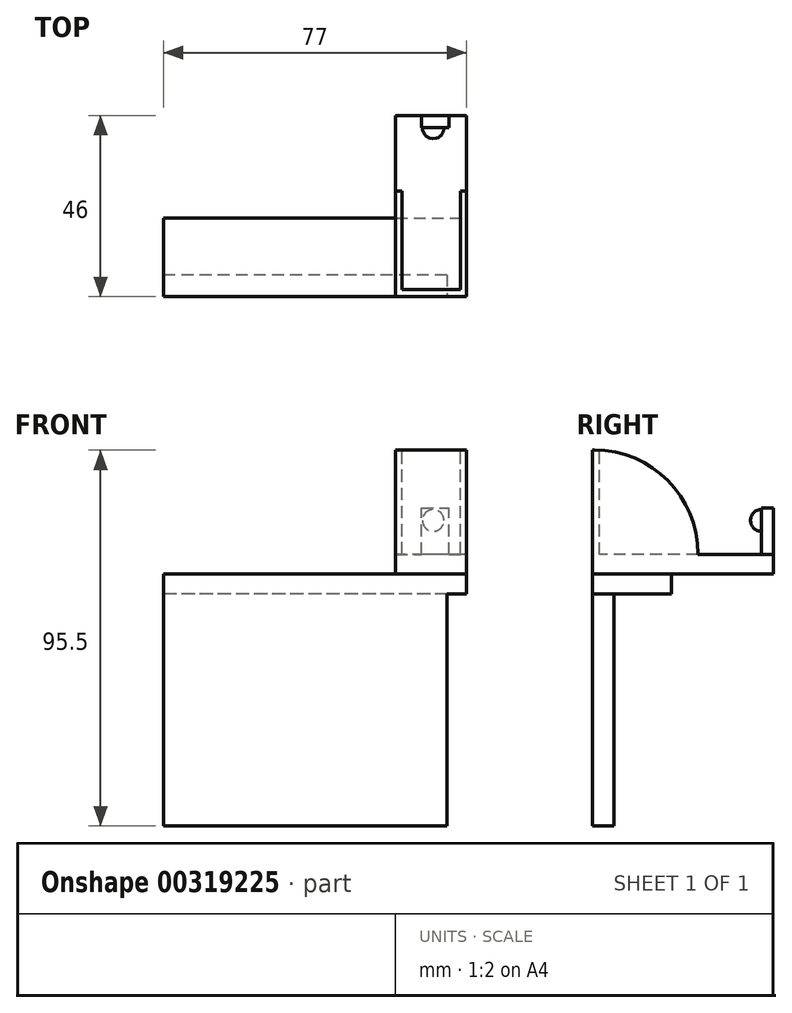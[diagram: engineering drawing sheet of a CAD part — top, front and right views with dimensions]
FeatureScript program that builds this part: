
annotation { "Feature Type Name" : "Feature", "Feature Type Description" : "" }
export const myFeature = defineFeature(function(context is Context, id is Id, definition is map)
    precondition{}
    {
        {
            var Q0;
            Q0=qCreatedBy(makeId("Top.planeOp"),FACE);
            var sketch = newSketch(context, id + "F0", { "sketchPlane" : qUnion([Q0])});
            skLineSegment(sketch, "E0.bottom", {"start": v(35.26, 25.04) * mm, "end": v(53.26, 25.04) * mm});
            skLineSegment(sketch, "E0.top", {"start": v(35.26, -20.96) * mm, "end": v(53.26, -20.96) * mm});
            skLineSegment(sketch, "E0.left", {"start": v(35.26, 25.04) * mm, "end": v(35.26, -20.96) * mm});
            skLineSegment(sketch, "E0.right", {"start": v(53.26, 25.04) * mm, "end": v(53.26, -20.96) * mm});
            skSolve(sketch);
        }
        {
            var Q0;
            Q0 = qSketchRegion(id + "F0", true);
            extrude(context, id + "F1", {"entities" : qUnion([Q0]), "depth" : 5 * mm});
        }
        {
            var Q0;
            Q0=makeQuery(id+"F1.opExtrude","CAP_FACE",FACE,{"disambiguationData":[OSD([sQuery(id+"F0.wireOp",EDGE,"E0.bottom"),sQuery(id+"F0.wireOp",EDGE,"E0.top"),sQuery(id+"F0.wireOp",EDGE,"E0.left"),sQuery(id+"F0.wireOp",EDGE,"E0.right")])],"isStart":false});
            var sketch = newSketch(context, id + "F2", { "sketchPlane" : qUnion([Q0])});
            skLineSegment(sketch, "E1.bottom", {"start": v(53.26, -20.96) * mm, "end": v(35.26, -20.96) * mm});
            skLineSegment(sketch, "E1.top", {"start": v(53.26, -19.13) * mm, "end": v(35.26, -19.13) * mm});
            skLineSegment(sketch, "E1.left", {"start": v(53.26, -20.96) * mm, "end": v(53.26, -19.13) * mm});
            skLineSegment(sketch, "E1.right", {"start": v(35.26, -20.96) * mm, "end": v(35.26, -19.13) * mm});
            skSolve(sketch);
        }
        {
            var Q0;
            Q0=makeQuery(id+"F2.imprint","IMPRINT",FACE,{"disambiguationData":[TD([[makeQuery(id+"F2.imprint","IMPRINT",EDGE,{"derivedFrom":sQuery(id+"F2.wireOp",EDGE,"E1.bottom")}),1.0]])]});
            extrude(context, id + "F3", {"entities" : qUnion([Q0]), "operationType" : NewBodyOperationType.ADD, "depth" : 26.5 * mm});
        }
        {
            var Q0;
            Q0=makeQuery(id+"F3.opExtrude","SWEPT_FACE",FACE,{"disambiguationData":[OSD([sQuery(id+"F2.wireOp",EDGE,"E1.top")])]});
            var sketch = newSketch(context, id + "F4", { "sketchPlane" : qUnion([Q0])});
            skLineSegment(sketch, "E2.bottom", {"start": v(-35.26, 5) * mm, "end": v(-36.8, 5) * mm});
            skLineSegment(sketch, "E2.top", {"start": v(-35.26, 31.5) * mm, "end": v(-36.8, 31.5) * mm});
            skLineSegment(sketch, "E2.left", {"start": v(-35.26, 5) * mm, "end": v(-35.26, 31.5) * mm});
            skLineSegment(sketch, "E2.right", {"start": v(-36.8, 5) * mm, "end": v(-36.8, 31.5) * mm});
            skLineSegment(sketch, "E3.bottom", {"start": v(-53.26, 5) * mm, "end": v(-51.68, 5) * mm});
            skLineSegment(sketch, "E3.top", {"start": v(-53.26, 31.5) * mm, "end": v(-51.68, 31.5) * mm});
            skLineSegment(sketch, "E3.left", {"start": v(-53.26, 5) * mm, "end": v(-53.26, 31.5) * mm});
            skLineSegment(sketch, "E3.right", {"start": v(-51.68, 5) * mm, "end": v(-51.68, 31.5) * mm});
            skSolve(sketch);
        }
        {
            var Q0;
            Q0 = qSketchRegion(id + "F4", true);
            extrude(context, id + "F5", {"entities" : qUnion([Q0]), "operationType" : NewBodyOperationType.ADD, "depth" : 25 * mm});
        }
        {
            var Q0;
            Q0=makeQuery(id+"F5.opExtrude","CAP_EDGE",EDGE,{"disambiguationData":[OSD([sQuery(id+"F4.wireOp",EDGE,"E2.top")])],"isStart":false});
            var Q1;
            Q1=makeQuery(id+"F5.opExtrude","CAP_EDGE",EDGE,{"disambiguationData":[OSD([sQuery(id+"F4.wireOp",EDGE,"E3.top")])],"isStart":false});
            fillet(context, id + "F6", {"entities" : qUnion([Q0, Q1]), "radius" : 26.36 * mm, "tangentPropagation" : true, "allowEdgeOverflow" : false});
        }
        {
            var Q0;
            Q0=makeQuery(id+"F1.opExtrude","SWEPT_FACE",FACE,{"disambiguationData":[OSD([sQuery(id+"F0.wireOp",EDGE,"E0.bottom")])]});
            var sketch = newSketch(context, id + "F7", { "sketchPlane" : qUnion([Q0])});
            skLineSegment(sketch, "E4.bottom", {"start": v(-41.81, 2.89) * mm, "end": v(-48.82, 2.89) * mm});
            skLineSegment(sketch, "E4.top", {"start": v(-41.81, 16.8) * mm, "end": v(-48.82, 16.8) * mm});
            skLineSegment(sketch, "E4.left", {"start": v(-41.81, 2.89) * mm, "end": v(-41.81, 16.8) * mm});
            skLineSegment(sketch, "E4.right", {"start": v(-48.82, 2.89) * mm, "end": v(-48.82, 16.8) * mm});
            skSolve(sketch);
        }
        {
            var Q0;
            {var subQ0=sQuery(id+"F7.wireOp",EDGE,"E4.bottom");Q0=makeQuery(id+"F7.imprint","IMPRINT",FACE,{"disambiguationData":[TD([[makeQuery(id+"F7.imprint","IMPRINT",EDGE,{"derivedFrom":subQ0}),-1.0]])]});}
            var Q1;
            {var subQ0=sQuery(id+"F7.wireOp",EDGE,"E4.top");Q1=makeQuery(id+"F7.imprint","IMPRINT",FACE,{"disambiguationData":[TD([[makeQuery(id+"F7.imprint","IMPRINT",EDGE,{"derivedFrom":subQ0}),1.0]])]});}
            extrude(context, id + "F8", {"entities" : qUnion([Q0, Q1]), "operationType" : NewBodyOperationType.ADD, "oppositeDirection" : true, "depth" : 3.1 * mm});
        }
        {
            var Q0;
            Q0=makeQuery(id+"F8.opExtrude","CAP_FACE",FACE,{"disambiguationData":[OSD([sQuery(id+"F7.wireOp",EDGE,"E4.bottom"),sQuery(id+"F7.wireOp",EDGE,"E4.top"),sQuery(id+"F7.wireOp",EDGE,"E4.left"),sQuery(id+"F7.wireOp",EDGE,"E4.right")])],"isStart":false});
            var sketch = newSketch(context, id + "F9", { "sketchPlane" : qUnion([Q0])});
            skCircle(sketch, "E5", {"center": v(44.8, 13.6) * mm, "radius": 2.73 * mm});
            skLineSegment(sketch, "E6", {"start": v(42.06, 13.64) * mm, "end": v(47.52, 13.64) * mm});
            skSolve(sketch);
        }
        {
            var Q0;
            {var subQ0=sQuery(id+"F9.wireOp",EDGE,"E6");Q0=makeQuery(id+"F9.imprint","IMPRINT",FACE,{"disambiguationData":[TD([[makeQuery(id+"F9.imprint","IMPRINT",EDGE,{"derivedFrom":subQ0}),-1.0]])]});}
            var Q1;
            Q1=sQuery(id+"F9.wireOp",EDGE,"E6");
            revolve(context, id + "F10", {"operationType" : NewBodyOperationType.ADD, "entities" : qUnion([Q0]), "axis" : qUnion([Q1]), "revolveType" : RevolveType.FULL});
        }
        {
            var Q0;
            Q0=makeQuery(id+"F3.boolean.opBoolean","MERGE",FACE,{"derivedFrom":[makeQuery(id+"F1.opExtrude","SWEPT_FACE",FACE,{"disambiguationData":[OSD([sQuery(id+"F0.wireOp",EDGE,"E0.top")])]}),makeQuery(id+"F3.opExtrude","SWEPT_FACE",FACE,{"disambiguationData":[OSD([sQuery(id+"F2.wireOp",EDGE,"E1.bottom")])]})]});
            var sketch = newSketch(context, id + "F11", { "sketchPlane" : qUnion([Q0])});
            skLineSegment(sketch, "E7.bottom", {"start": v(53.26, 0) * mm, "end": v(-23.74, 0) * mm});
            skLineSegment(sketch, "E7.top", {"start": v(53.26, -64) * mm, "end": v(-23.74, -64) * mm});
            skLineSegment(sketch, "E7.left", {"start": v(53.26, 0) * mm, "end": v(53.26, -64) * mm});
            skLineSegment(sketch, "E7.right", {"start": v(-23.74, 0) * mm, "end": v(-23.74, -64) * mm});
            skLineSegment(sketch, "E8.top", {"start": v(53.26, -5) * mm, "end": v(-23.74, -5) * mm});
            skLineSegment(sketch, "E8.left", {"start": v(53.26, 0) * mm, "end": v(53.26, -5) * mm});
            skLineSegment(sketch, "E8.right", {"start": v(-23.74, 0) * mm, "end": v(-23.74, -5) * mm});
            skLineSegment(sketch, "E9.bottom", {"start": v(53.26, -5) * mm, "end": v(48.26, -5) * mm});
            skLineSegment(sketch, "E9.top", {"start": v(53.26, -64) * mm, "end": v(48.26, -64) * mm});
            skLineSegment(sketch, "E9.left", {"start": v(53.26, -5) * mm, "end": v(53.26, -64) * mm});
            skLineSegment(sketch, "E9.right", {"start": v(48.26, -5) * mm, "end": v(48.26, -64) * mm});
            skLineSegment(sketch, "E10.bottom", {"start": v(48.26, -64) * mm, "end": v(-23.74, -64) * mm});
            skLineSegment(sketch, "E10.top", {"start": v(48.26, -59) * mm, "end": v(-23.74, -59) * mm});
            skLineSegment(sketch, "E10.left", {"start": v(48.26, -64) * mm, "end": v(48.26, -59) * mm});
            skLineSegment(sketch, "E10.right", {"start": v(-23.74, -64) * mm, "end": v(-23.74, -59) * mm});
            skSolve(sketch);
        }
        {
            var Q0;
            Q0=makeQuery(id+"F11.imprint","IMPRINT",FACE,{"disambiguationData":[TD([[makeQuery(id+"F11.imprint","IMPRINT",EDGE,{"derivedFrom":sQuery(id+"F11.wireOp",EDGE,"E10.bottom")}),-1.0]])]});
            var Q1;
            Q1=makeQuery(id+"F11.imprint","IMPRINT",FACE,{"disambiguationData":[TD([[makeQuery(id+"F11.imprint","IMPRINT",EDGE,{"derivedFrom":sQuery(id+"F11.wireOp",EDGE,"E9.bottom")}),1.0]])]});
            var Q2;
            Q2=makeQuery(id+"F11.imprint","IMPRINT",FACE,{"disambiguationData":[TD([[makeQuery(id+"F11.imprint","IMPRINT",EDGE,{"derivedFrom":sQuery(id+"F11.wireOp",EDGE,"E8.top")}),-1.0]])]});
            extrude(context, id + "F12", {"entities" : qUnion([Q0, Q1, Q2]), "oppositeDirection" : true, "depth" : 20 * mm});
        }
        {
            var Q0;
            Q0=makeQuery(id+"F11.imprint","IMPRINT",FACE,{"disambiguationData":[TD([[makeQuery(id+"F11.imprint","IMPRINT",EDGE,{"derivedFrom":sQuery(id+"F11.wireOp",EDGE,"E7.right")}),1.0]])]});
            extrude(context, id + "F13", {"entities" : qUnion([Q0]), "operationType" : NewBodyOperationType.ADD, "oppositeDirection" : true, "depth" : 5.5 * mm});
        }
    });
